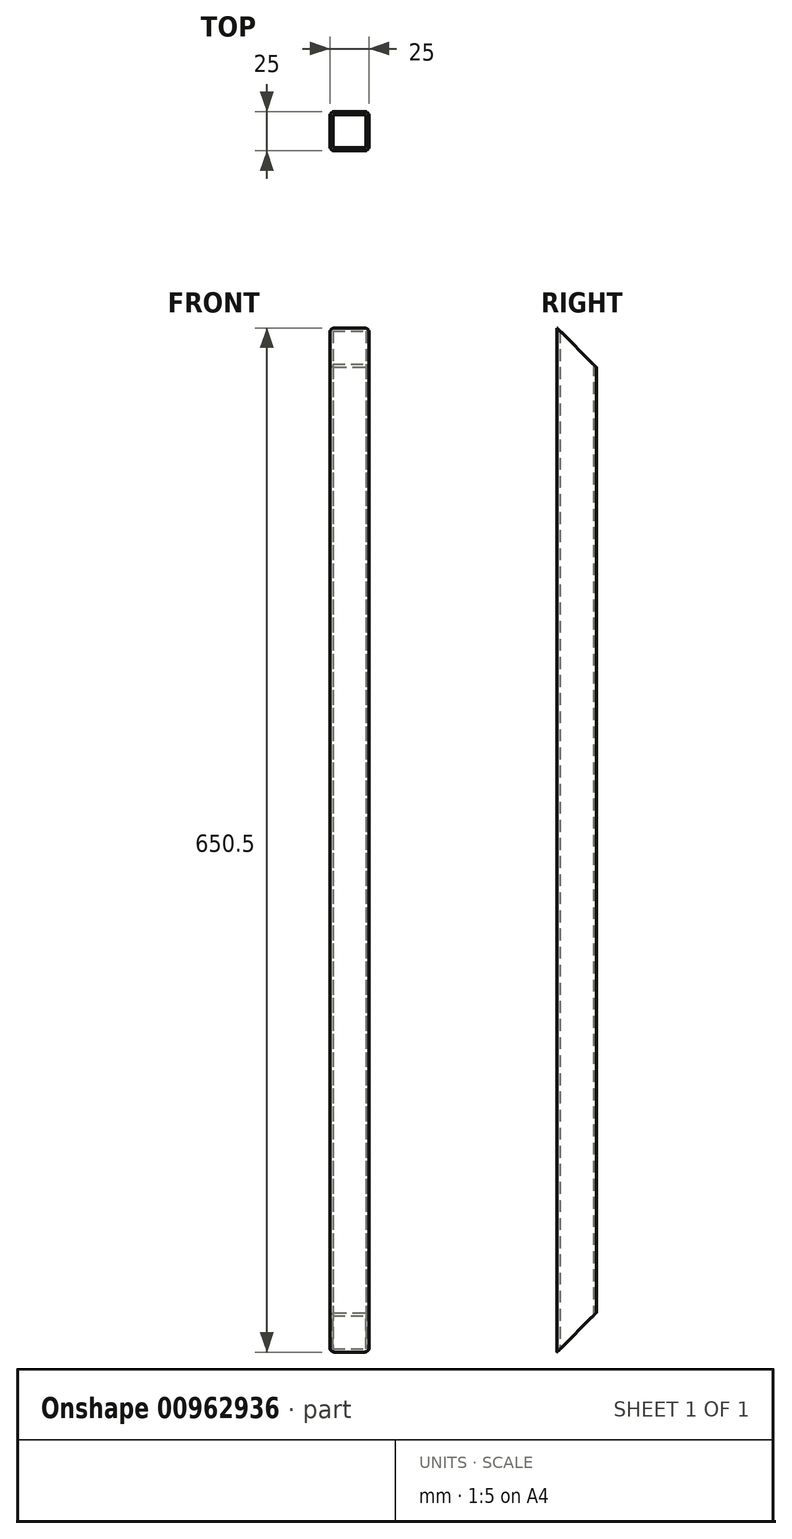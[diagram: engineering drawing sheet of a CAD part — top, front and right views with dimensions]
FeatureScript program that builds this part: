
annotation { "Feature Type Name" : "Feature", "Feature Type Description" : "" }
export const myFeature = defineFeature(function(context is Context, id is Id, definition is map)
    precondition{}
    {
        {
            var Q0;
            Q0=qCreatedBy(makeId("Top.planeOp"),FACE);
            var sketch = newSketch(context, id + "F0", { "sketchPlane" : qUnion([Q0])});
            skLineSegment(sketch, "E0.bottom", {"start": v(9.5, 12.5) * mm, "end": v(-9.5, 12.5) * mm});
            skLineSegment(sketch, "E0.top", {"start": v(9.5, -12.5) * mm, "end": v(-9.5, -12.5) * mm});
            skLineSegment(sketch, "E0.left", {"start": v(12.5, 9.5) * mm, "end": v(12.5, -9.5) * mm});
            skLineSegment(sketch, "E0.right", {"start": v(-12.5, 9.5) * mm, "end": v(-12.5, -9.5) * mm});
            skPoint(sketch, "E0.middle", {"position": v(0, 0) * mm});
            skPoint(sketch, "E1.visualSharp", {"position": v(-12.5, 12.5) * mm});
            skArc(sketch, "E1.filletArc", {"start": v(-9.5, 12.5) * mm, "mid": v(-11.62, 11.62) * mm, "end": v(-12.5, 9.5) * mm});
            skPoint(sketch, "E2.visualSharp", {"position": v(-12.5, -12.5) * mm});
            skArc(sketch, "E2.filletArc", {"start": v(-12.5, -9.5) * mm, "mid": v(-11.62, -11.62) * mm, "end": v(-9.5, -12.5) * mm});
            skPoint(sketch, "E3.visualSharp", {"position": v(12.5, -12.5) * mm});
            skArc(sketch, "E3.filletArc", {"start": v(9.5, -12.5) * mm, "mid": v(11.62, -11.62) * mm, "end": v(12.5, -9.5) * mm});
            skPoint(sketch, "E4.visualSharp", {"position": v(12.5, 12.5) * mm});
            skArc(sketch, "E4.filletArc", {"start": v(12.5, 9.5) * mm, "mid": v(11.62, 11.62) * mm, "end": v(9.5, 12.5) * mm});
            skLineSegment(sketch, "E5.0", {"start": v(10.5, 10.5) * mm, "end": v(-10.5, 10.5) * mm});
            skLineSegment(sketch, "E5.1", {"start": v(10.5, 10.5) * mm, "end": v(10.5, -10.5) * mm});
            skLineSegment(sketch, "E5.2", {"start": v(10.5, -10.5) * mm, "end": v(-10.5, -10.5) * mm});
            skLineSegment(sketch, "E5.3", {"start": v(-10.5, 10.5) * mm, "end": v(-10.5, -10.5) * mm});
            skSolve(sketch);
        }
        {
            var Q0;
            Q0=makeQuery(id+"F0.imprint","IMPRINT",FACE,{"disambiguationData":[TD([[makeQuery(id+"F0.imprint","IMPRINT",EDGE,{"derivedFrom":sQuery(id+"F0.wireOp",EDGE,"E0.bottom")}),1.0]])]});
            extrude(context, id + "F1", {"entities" : qUnion([Q0]), "depth" : 680 * mm, "offsetDistance" : 25 * mm});
        }
        {
            var Q0;
            Q0=qCreatedBy(makeId("Right.planeOp"),FACE);
            var sketch = newSketch(context, id + "F2", { "sketchPlane" : qUnion([Q0])});
            skLineSegment(sketch, "E6", {"start": v(-12.5, 0) * mm, "end": v(12.5, 25) * mm});
            skLineSegment(sketch, "E7", {"start": v(12.5, 25) * mm, "end": v(12.5, 0) * mm});
            skLineSegment(sketch, "E8", {"start": v(12.5, 0) * mm, "end": v(-12.5, 0) * mm});
            skLineSegment(sketch, "E9", {"start": v(12.5, 625.5) * mm, "end": v(12.5, 680) * mm});
            skLineSegment(sketch, "E10", {"start": v(12.5, 680) * mm, "end": v(-12.5, 680) * mm});
            skLineSegment(sketch, "E11", {"start": v(-12.5, 680) * mm, "end": v(-12.5, 650.5) * mm});
            skLineSegment(sketch, "E12", {"start": v(-12.5, 650.5) * mm, "end": v(12.5, 625.5) * mm});
            skSolve(sketch);
        }
        {
            var Q0;
            Q0=qSketchRegion(id+"F2",true);
            extrude(context, id + "F3", {"entities" : qUnion([Q0]), "operationType" : NewBodyOperationType.REMOVE, "endBound" : BoundingType.SYMMETRIC, "oppositeDirection" : true, "depth" : 25 * mm, "offsetDistance" : 25 * mm});
        }
    });
